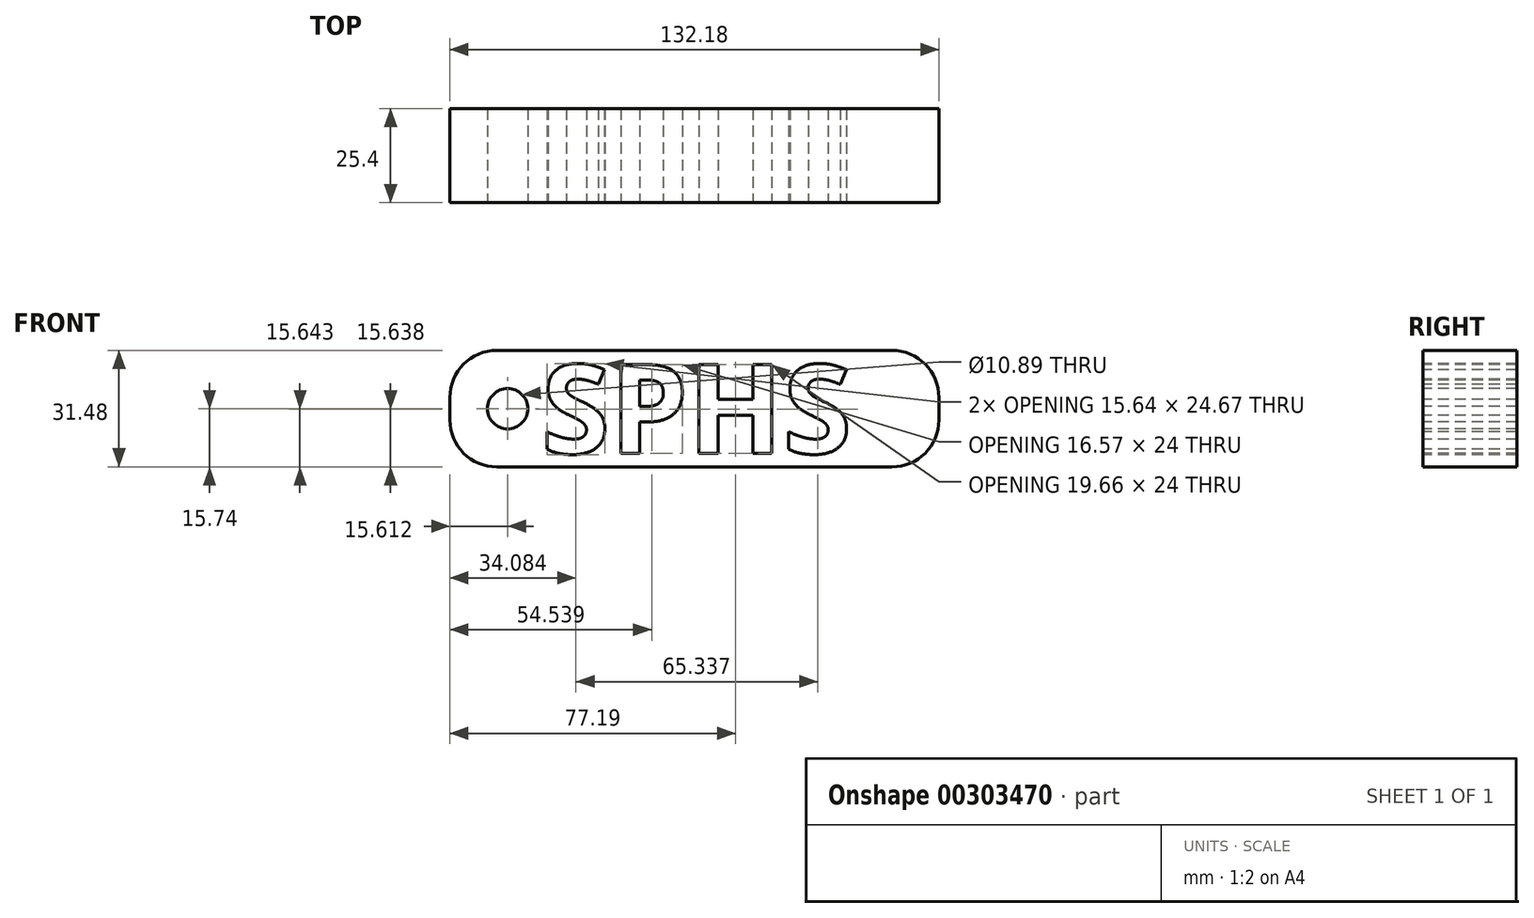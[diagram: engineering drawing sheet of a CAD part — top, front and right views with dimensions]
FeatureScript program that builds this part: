
annotation { "Feature Type Name" : "Feature", "Feature Type Description" : "" }
export const myFeature = defineFeature(function(context is Context, id is Id, definition is map)
    precondition{}
    {
        {
            var Q0;
            Q0=qCreatedBy(makeId("Front.planeOp"),FACE);
            var sketch = newSketch(context, id + "F0", { "sketchPlane" : qUnion([Q0])});
            skLineSegment(sketch, "E0.bottom", {"start": v(-66.09, 15.74) * mm, "end": v(66.09, 15.74) * mm});
            skLineSegment(sketch, "E0.top", {"start": v(-66.09, -15.74) * mm, "end": v(66.09, -15.74) * mm});
            skLineSegment(sketch, "E0.left", {"start": v(-66.09, 15.74) * mm, "end": v(-66.09, -15.74) * mm});
            skLineSegment(sketch, "E0.right", {"start": v(66.09, 15.74) * mm, "end": v(66.09, -15.74) * mm});
            skPoint(sketch, "E0.middle", {"position": v(0, 0) * mm});
            skSolve(sketch);
        }
        {
            var Q0;
            Q0=makeQuery(id+"F0.imprint","IMPRINT",FACE,{"disambiguationData":[TD([[makeQuery(id+"F0.imprint","IMPRINT",EDGE,{"derivedFrom":sQuery(id+"F0.wireOp",EDGE,"E0.bottom")}),-1.0]])]});
            extrude(context, id + "F1", {"entities" : qUnion([Q0]), "depth" : 25.4 * mm});
        }
        {
            var Q0;
            Q0=makeQuery(id+"F1.opExtrude","CAP_FACE",FACE,{"disambiguationData":[OSD([sQuery(id+"F0.wireOp",EDGE,"E0.bottom"),sQuery(id+"F0.wireOp",EDGE,"E0.top"),sQuery(id+"F0.wireOp",EDGE,"E0.left"),sQuery(id+"F0.wireOp",EDGE,"E0.right")])],"isStart":false});
            var sketch = newSketch(context, id + "F2", { "sketchPlane" : qUnion([Q0])});
            skText(sketch, "E1", { "text": "SPHS", "fontName": "OpenSans-Bold.ttf"});
            const initialGuessF2  = {"E1": [-0.04137, -0.0121, 1, 0, 0.0242]};
            skSetInitialGuess(sketch, initialGuessF2);
            skSolve(sketch);
        }
        {
            var Q0;
            Q0 = qSketchRegion(id + "F2", true);
            extrude(context, id + "F3", {"entities" : qUnion([Q0]), "operationType" : NewBodyOperationType.REMOVE, "oppositeDirection" : true, "depth" : 25.4 * mm});
        }
        {
            var Q0;
            Q0=makeQuery(id+"F1.opExtrude","SWEPT_EDGE",EDGE,{"disambiguationData":[OSD([sQuery(id+"F0.wireOp",EDGE,"E0.bottom"),sQuery(id+"F0.wireOp",EDGE,"E0.right")])]});
            fillet(context, id + "F4", {"entities" : qUnion([Q0]), "radius" : 12.7 * mm, "tangentPropagation" : true, "allowEdgeOverflow" : false});
        }
        {
            var Q0;
            Q0=makeQuery(id+"F1.opExtrude","SWEPT_EDGE",EDGE,{"disambiguationData":[OSD([sQuery(id+"F0.wireOp",EDGE,"E0.top"),sQuery(id+"F0.wireOp",EDGE,"E0.right")])]});
            fillet(context, id + "F5", {"entities" : qUnion([Q0]), "radius" : 12.7 * mm, "tangentPropagation" : true, "allowEdgeOverflow" : false});
        }
        {
            var Q0;
            Q0=makeQuery(id+"F1.opExtrude","SWEPT_EDGE",EDGE,{"disambiguationData":[OSD([sQuery(id+"F0.wireOp",EDGE,"E0.bottom"),sQuery(id+"F0.wireOp",EDGE,"E0.left")])]});
            fillet(context, id + "F6", {"entities" : qUnion([Q0]), "radius" : 12.7 * mm, "tangentPropagation" : true, "allowEdgeOverflow" : false});
        }
        {
            var Q0;
            Q0=makeQuery(id+"F1.opExtrude","SWEPT_EDGE",EDGE,{"disambiguationData":[OSD([sQuery(id+"F0.wireOp",EDGE,"E0.top"),sQuery(id+"F0.wireOp",EDGE,"E0.left")])]});
            fillet(context, id + "F7", {"entities" : qUnion([Q0]), "radius" : 12.7 * mm, "tangentPropagation" : true, "allowEdgeOverflow" : false});
        }
        {
            var Q0;
            {var subQ0=sQuery(id+"F0.wireOp",EDGE,"E0.left");var subQ1=sQuery(id+"F0.wireOp",EDGE,"E0.bottom");var subQ2=sQuery(id+"F0.wireOp",EDGE,"E0.right");var subQ3=sQuery(id+"F0.wireOp",EDGE,"E0.top");Q0=makeQuery(id+"F3.boolean.opBoolean","SPLIT",FACE,{"disambiguationData":[TD([makeQuery(id+"F1.opExtrude","SWEPT_FACE",FACE,{"disambiguationData":[OSD([subQ1])]})])],"derivedFrom":makeQuery(id+"F1.opExtrude","CAP_FACE",FACE,{"disambiguationData":[OSD([subQ1,subQ3,subQ0,subQ2])],"isStart":false})});}
            var sketch = newSketch(context, id + "F8", { "sketchPlane" : qUnion([Q0])});
            skCircle(sketch, "E2", {"center": v(-50.48, 0) * mm, "radius": 5.45 * mm});
            skSolve(sketch);
        }
        {
            var Q0;
            Q0=makeQuery(id+"F8.imprint","IMPRINT",FACE,{"disambiguationData":[TD([[makeQuery(id+"F8.imprint","IMPRINT",EDGE,{"derivedFrom":sQuery(id+"F8.wireOp",EDGE,"E2")}),1.0]])]});
            extrude(context, id + "F9", {"entities" : qUnion([Q0]), "operationType" : NewBodyOperationType.REMOVE, "endBound" : BoundingType.THROUGH_ALL, "oppositeDirection" : true, "depth" : 25.4 * mm});
        }
    });
